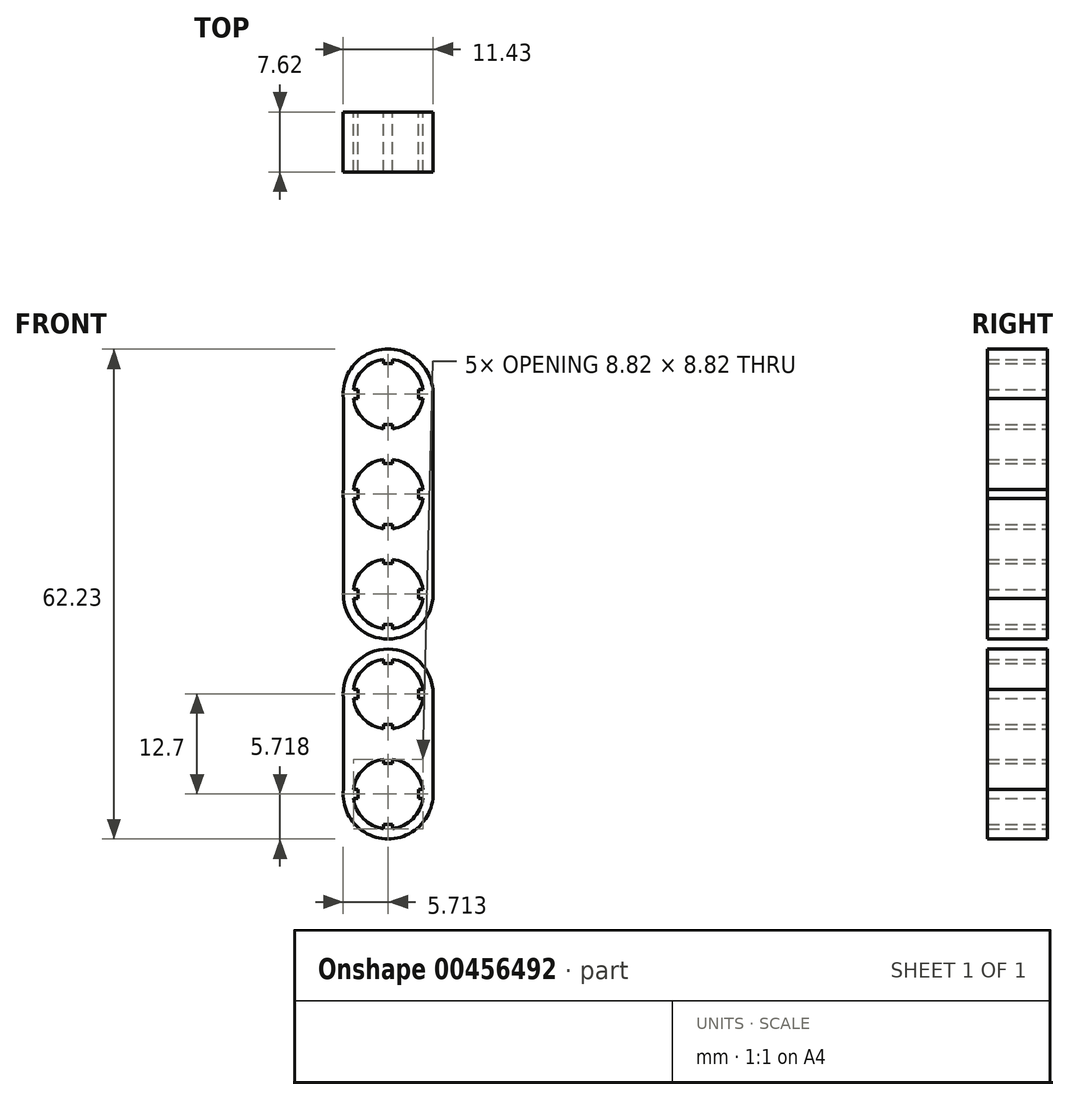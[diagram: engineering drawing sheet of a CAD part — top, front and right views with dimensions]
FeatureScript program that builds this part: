
annotation { "Feature Type Name" : "Feature", "Feature Type Description" : "" }
export const myFeature = defineFeature(function(context is Context, id is Id, definition is map)
    precondition{}
    {
        {
            var Q0;
            Q0=qCreatedBy(makeId("Front.planeOp"),FACE);
            var sketch = newSketch(context, id + "F0", { "sketchPlane" : qUnion([Q0])});
            skCircle(sketch, "E0", {"center": v(-13.53, 8.26) * mm, "radius": 4.45 * mm});
            skCircle(sketch, "E1", {"center": v(-13.53, -4.44) * mm, "radius": 4.45 * mm});
            skCircle(sketch, "E2", {"center": v(-13.53, -17.14) * mm, "radius": 4.45 * mm});
            skCircle(sketch, "E3", {"center": v(-13.53, -29.84) * mm, "radius": 4.45 * mm});
            skCircle(sketch, "E4", {"center": v(-13.53, -42.54) * mm, "radius": 4.45 * mm});
            skCircle(sketch, "E5", {"center": v(-13.53, 8.26) * mm, "radius": 5.72 * mm});
            skCircle(sketch, "E6", {"center": v(-13.53, -4.44) * mm, "radius": 5.72 * mm});
            skCircle(sketch, "E7", {"center": v(-13.53, -17.14) * mm, "radius": 5.72 * mm});
            skCircle(sketch, "E8", {"center": v(-13.53, -29.84) * mm, "radius": 5.72 * mm});
            skCircle(sketch, "E9", {"center": v(-13.53, -42.54) * mm, "radius": 5.72 * mm});
            skLineSegment(sketch, "E10", {"start": v(-18.03, 8.83) * mm, "end": v(-17.38, 8.83) * mm});
            skLineSegment(sketch, "E11", {"start": v(-17.38, 8.83) * mm, "end": v(-17.38, 7.69) * mm});
            skLineSegment(sketch, "E12", {"start": v(-17.38, 7.69) * mm, "end": v(-17.94, 7.69) * mm});
            skLineSegment(sketch, "E13", {"start": v(-9.12, -41.97) * mm, "end": v(-9.68, -41.97) * mm});
            skLineSegment(sketch, "E14", {"start": v(-9.68, -41.97) * mm, "end": v(-9.68, -43.11) * mm});
            skLineSegment(sketch, "E15", {"start": v(-9.68, -43.11) * mm, "end": v(-9.12, -43.11) * mm});
            skLineSegment(sketch, "E16", {"start": v(-9.12, 8.83) * mm, "end": v(-9.68, 8.83) * mm});
            skLineSegment(sketch, "E17", {"start": v(-9.68, 8.83) * mm, "end": v(-9.68, 7.69) * mm});
            skLineSegment(sketch, "E18", {"start": v(-9.68, 7.69) * mm, "end": v(-9.12, 7.69) * mm});
            skLineSegment(sketch, "E19", {"start": v(-14.1, 12.67) * mm, "end": v(-14.1, 12.1) * mm});
            skLineSegment(sketch, "E20", {"start": v(-14.1, 12.1) * mm, "end": v(-12.96, 12.1) * mm});
            skLineSegment(sketch, "E21", {"start": v(-12.96, 12.1) * mm, "end": v(-12.96, 12.67) * mm});
            skLineSegment(sketch, "E22", {"start": v(-14.1, 3.85) * mm, "end": v(-14.1, 4.4) * mm});
            skLineSegment(sketch, "E23", {"start": v(-14.1, 4.4) * mm, "end": v(-12.96, 4.4) * mm});
            skLineSegment(sketch, "E24", {"start": v(-12.96, 4.4) * mm, "end": v(-12.96, 3.85) * mm});
            skLineSegment(sketch, "E25", {"start": v(-14.1, -0.03) * mm, "end": v(-14.1, -0.6) * mm});
            skLineSegment(sketch, "E26", {"start": v(-14.1, -0.6) * mm, "end": v(-12.96, -0.6) * mm});
            skLineSegment(sketch, "E27", {"start": v(-12.96, -0.6) * mm, "end": v(-12.96, -0.03) * mm});
            skLineSegment(sketch, "E28", {"start": v(-14.1, -8.85) * mm, "end": v(-14.1, -8.3) * mm});
            skLineSegment(sketch, "E29", {"start": v(-14.1, -8.3) * mm, "end": v(-12.96, -8.3) * mm});
            skLineSegment(sketch, "E30", {"start": v(-12.96, -8.3) * mm, "end": v(-12.96, -8.85) * mm});
            skLineSegment(sketch, "E31", {"start": v(-17.94, -3.87) * mm, "end": v(-17.38, -3.87) * mm});
            skLineSegment(sketch, "E32", {"start": v(-17.38, -3.87) * mm, "end": v(-17.38, -5.01) * mm});
            skLineSegment(sketch, "E33", {"start": v(-17.38, -5.01) * mm, "end": v(-17.94, -5.01) * mm});
            skLineSegment(sketch, "E34", {"start": v(-9.12, -3.87) * mm, "end": v(-9.68, -3.87) * mm});
            skLineSegment(sketch, "E35", {"start": v(-9.68, -3.87) * mm, "end": v(-9.68, -5.01) * mm});
            skLineSegment(sketch, "E36", {"start": v(-9.68, -5.01) * mm, "end": v(-9.12, -5.01) * mm});
            skLineSegment(sketch, "E37", {"start": v(-14.1, -12.73) * mm, "end": v(-14.1, -13.3) * mm});
            skLineSegment(sketch, "E38", {"start": v(-14.1, -13.3) * mm, "end": v(-12.96, -13.3) * mm});
            skLineSegment(sketch, "E39", {"start": v(-12.96, -13.3) * mm, "end": v(-12.96, -12.73) * mm});
            skLineSegment(sketch, "E40", {"start": v(-14.1, -21.55) * mm, "end": v(-14.1, -21) * mm});
            skLineSegment(sketch, "E41", {"start": v(-14.1, -21) * mm, "end": v(-12.96, -21) * mm});
            skLineSegment(sketch, "E42", {"start": v(-12.96, -21) * mm, "end": v(-12.96, -21.55) * mm});
            skLineSegment(sketch, "E43", {"start": v(-17.94, -16.57) * mm, "end": v(-17.38, -16.57) * mm});
            skLineSegment(sketch, "E44", {"start": v(-17.38, -16.57) * mm, "end": v(-17.38, -17.71) * mm});
            skLineSegment(sketch, "E45", {"start": v(-17.38, -17.71) * mm, "end": v(-17.94, -17.71) * mm});
            skLineSegment(sketch, "E46", {"start": v(-9.12, -16.57) * mm, "end": v(-9.68, -16.57) * mm});
            skLineSegment(sketch, "E47", {"start": v(-9.68, -16.57) * mm, "end": v(-9.68, -17.71) * mm});
            skLineSegment(sketch, "E48", {"start": v(-9.68, -17.71) * mm, "end": v(-9.12, -17.71) * mm});
            skLineSegment(sketch, "E49", {"start": v(-14.1, -25.43) * mm, "end": v(-14.1, -26) * mm});
            skLineSegment(sketch, "E50", {"start": v(-14.1, -26) * mm, "end": v(-12.96, -26) * mm});
            skLineSegment(sketch, "E51", {"start": v(-12.96, -26) * mm, "end": v(-12.96, -25.43) * mm});
            skLineSegment(sketch, "E52", {"start": v(-14.1, -34.25) * mm, "end": v(-14.1, -33.7) * mm});
            skLineSegment(sketch, "E53", {"start": v(-14.1, -33.7) * mm, "end": v(-12.96, -33.7) * mm});
            skLineSegment(sketch, "E54", {"start": v(-12.96, -33.7) * mm, "end": v(-12.96, -34.25) * mm});
            skLineSegment(sketch, "E55", {"start": v(-17.94, -29.27) * mm, "end": v(-17.38, -29.27) * mm});
            skLineSegment(sketch, "E56", {"start": v(-17.38, -29.27) * mm, "end": v(-17.38, -30.41) * mm});
            skLineSegment(sketch, "E57", {"start": v(-17.38, -30.41) * mm, "end": v(-17.94, -30.41) * mm});
            skLineSegment(sketch, "E58", {"start": v(-9.12, -29.27) * mm, "end": v(-9.68, -29.27) * mm});
            skLineSegment(sketch, "E59", {"start": v(-9.68, -29.27) * mm, "end": v(-9.68, -30.41) * mm});
            skLineSegment(sketch, "E60", {"start": v(-9.68, -30.41) * mm, "end": v(-9.12, -30.41) * mm});
            skLineSegment(sketch, "E61", {"start": v(-17.94, -41.97) * mm, "end": v(-17.38, -41.97) * mm});
            skLineSegment(sketch, "E62", {"start": v(-17.38, -41.97) * mm, "end": v(-17.38, -43.11) * mm});
            skLineSegment(sketch, "E63", {"start": v(-17.38, -43.11) * mm, "end": v(-17.94, -43.11) * mm});
            skLineSegment(sketch, "E64", {"start": v(-14.1, -38.13) * mm, "end": v(-14.1, -38.7) * mm});
            skLineSegment(sketch, "E65", {"start": v(-14.1, -38.7) * mm, "end": v(-12.96, -38.7) * mm});
            skLineSegment(sketch, "E66", {"start": v(-12.96, -38.7) * mm, "end": v(-12.96, -38.13) * mm});
            skLineSegment(sketch, "E67", {"start": v(-14.1, -46.95) * mm, "end": v(-14.1, -46.4) * mm});
            skLineSegment(sketch, "E68", {"start": v(-14.1, -46.4) * mm, "end": v(-12.96, -46.4) * mm});
            skLineSegment(sketch, "E69", {"start": v(-12.96, -46.4) * mm, "end": v(-12.96, -46.95) * mm});
            skLineSegment(sketch, "E70", {"start": v(-19.21, 8.83) * mm, "end": v(-19.21, -42.54) * mm});
            skLineSegment(sketch, "E71", {"start": v(-19.21, -42.54) * mm, "end": v(-19.32, -43.49) * mm});
            skLineSegment(sketch, "E72", {"start": v(-7.84, 8.83) * mm, "end": v(-7.84, -43.11) * mm});
            skLineSegment(sketch, "E73", {"start": v(-7.84, -43.11) * mm, "end": v(-7.23, -42.43) * mm});
            skSolve(sketch);
        }
        {
            var Q0;
            {var subQ0=sQuery(id+"F0.wireOp",EDGE,"E70");var subQ1=sQuery(id+"F0.wireOp",EDGE,"E6");var subQ2=makeQuery(id+"F0.imprint","INTERSECT",VERTEX,{"disambiguationData":[OD(1.0)],"derivedFrom":[subQ1,subQ0]});Q0=makeQuery(id+"F0.imprint","IMPRINT",FACE,{"disambiguationData":[TD([[makeQuery(id+"F0.imprint","IMPRINT",EDGE,{"disambiguationData":[TD([[subQ2,-1.0]])],"derivedFrom":subQ1}),-1.0]])]});}
            var Q1;
            {var subQ0=sQuery(id+"F0.wireOp",EDGE,"E1");var subQ11=makeQuery(id+"F0.imprint","INTERSECT",VERTEX,{"derivedFrom":[subQ0,sQuery(id+"F0.wireOp",EDGE,"E27")]});Q1=makeQuery(id+"F0.imprint","IMPRINT",FACE,{"disambiguationData":[TD([[makeQuery(id+"F0.imprint","IMPRINT",EDGE,{"disambiguationData":[TD([[subQ11,1.0]])],"derivedFrom":subQ0}),-1.0]])]});}
            var Q2;
            {var subQ0=sQuery(id+"F0.wireOp",EDGE,"E70");var subQ1=sQuery(id+"F0.wireOp",EDGE,"E8");var subQ2=makeQuery(id+"F0.imprint","INTERSECT",VERTEX,{"disambiguationData":[OD(1.0)],"derivedFrom":[subQ1,subQ0]});Q2=makeQuery(id+"F0.imprint","IMPRINT",FACE,{"disambiguationData":[TD([[makeQuery(id+"F0.imprint","IMPRINT",EDGE,{"disambiguationData":[TD([[subQ2,-1.0]])],"derivedFrom":subQ1}),-1.0]])]});}
            var Q3;
            {var subQ5=sQuery(id+"F0.wireOp",EDGE,"E3");var subQ13=makeQuery(id+"F0.imprint","INTERSECT",VERTEX,{"derivedFrom":[subQ5,sQuery(id+"F0.wireOp",EDGE,"E51")]});Q3=makeQuery(id+"F0.imprint","IMPRINT",FACE,{"disambiguationData":[TD([[makeQuery(id+"F0.imprint","IMPRINT",EDGE,{"disambiguationData":[TD([[subQ13,1.0]])],"derivedFrom":subQ5}),-1.0]])]});}
            var Q4;
            {var subQ0=sQuery(id+"F0.wireOp",EDGE,"E70");var subQ1=sQuery(id+"F0.wireOp",EDGE,"E5");var subQ2=makeQuery(id+"F0.imprint","INTERSECT",VERTEX,{"disambiguationData":[OD(1.0)],"derivedFrom":[subQ1,subQ0]});Q4=makeQuery(id+"F0.imprint","IMPRINT",FACE,{"disambiguationData":[TD([[makeQuery(id+"F0.imprint","IMPRINT",EDGE,{"disambiguationData":[TD([[subQ2,-1.0]])],"derivedFrom":subQ1}),-1.0]])]});}
            var Q5;
            {var subQ0=sQuery(id+"F0.wireOp",EDGE,"E70");var subQ1=sQuery(id+"F0.wireOp",EDGE,"E7");var subQ2=makeQuery(id+"F0.imprint","INTERSECT",VERTEX,{"disambiguationData":[OD(1.0)],"derivedFrom":[subQ1,subQ0]});Q5=makeQuery(id+"F0.imprint","IMPRINT",FACE,{"disambiguationData":[TD([[makeQuery(id+"F0.imprint","IMPRINT",EDGE,{"disambiguationData":[TD([[subQ2,-1.0]])],"derivedFrom":subQ1}),-1.0]])]});}
            var Q6;
            {var subQ5=sQuery(id+"F0.wireOp",EDGE,"E2");var subQ11=makeQuery(id+"F0.imprint","INTERSECT",VERTEX,{"derivedFrom":[subQ5,sQuery(id+"F0.wireOp",EDGE,"E39")]});Q6=makeQuery(id+"F0.imprint","IMPRINT",FACE,{"disambiguationData":[TD([[makeQuery(id+"F0.imprint","IMPRINT",EDGE,{"disambiguationData":[TD([[subQ11,1.0]])],"derivedFrom":subQ5}),-1.0]])]});}
            var Q7;
            {var subQ7=sQuery(id+"F0.wireOp",EDGE,"E0");var subQ8=makeQuery(id+"F0.imprint","INTERSECT",VERTEX,{"derivedFrom":[subQ7,sQuery(id+"F0.wireOp",EDGE,"E16")]});Q7=makeQuery(id+"F0.imprint","IMPRINT",FACE,{"disambiguationData":[TD([[makeQuery(id+"F0.imprint","IMPRINT",EDGE,{"disambiguationData":[TD([[subQ8,-1.0]])],"derivedFrom":subQ7}),-1.0]])]});}
            var Q8;
            {var subQ0=sQuery(id+"F0.wireOp",EDGE,"E4");var subQ1=makeQuery(id+"F0.imprint","INTERSECT",VERTEX,{"derivedFrom":[subQ0,sQuery(id+"F0.wireOp",EDGE,"E13")]});Q8=makeQuery(id+"F0.imprint","IMPRINT",FACE,{"disambiguationData":[TD([[makeQuery(id+"F0.imprint","IMPRINT",EDGE,{"disambiguationData":[TD([[subQ1,-1.0]])],"derivedFrom":subQ0}),-1.0]])]});}
            var Q9;
            {var subQ0=sQuery(id+"F0.wireOp",EDGE,"E49");Q9=makeQuery(id+"F0.imprint","IMPRINT",FACE,{"disambiguationData":[TD([[makeQuery(id+"F0.imprint","IMPRINT",EDGE,{"derivedFrom":subQ0}),1.0]])]});}
            var Q10;
            {var subQ0=sQuery(id+"F0.wireOp",EDGE,"E70");var subQ1=sQuery(id+"F0.wireOp",EDGE,"E5");var subQ2=makeQuery(id+"F0.imprint","INTERSECT",VERTEX,{"disambiguationData":[OD(0.0)],"derivedFrom":[subQ1,subQ0]});Q10=makeQuery(id+"F0.imprint","IMPRINT",FACE,{"disambiguationData":[TD([[makeQuery(id+"F0.imprint","IMPRINT",EDGE,{"disambiguationData":[TD([[subQ2,-1.0]])],"derivedFrom":subQ1}),1.0]])]});}
            var Q11;
            {var subQ0=sQuery(id+"F0.wireOp",EDGE,"E72");var subQ1=sQuery(id+"F0.wireOp",EDGE,"E5");var subQ2=makeQuery(id+"F0.imprint","INTERSECT",VERTEX,{"disambiguationData":[OD(0.0)],"derivedFrom":[subQ1,subQ0]});Q11=makeQuery(id+"F0.imprint","IMPRINT",FACE,{"disambiguationData":[TD([[makeQuery(id+"F0.imprint","IMPRINT",EDGE,{"disambiguationData":[TD([[subQ2,1.0]])],"derivedFrom":subQ1}),1.0]])]});}
            var Q12;
            {var subQ0=sQuery(id+"F0.wireOp",EDGE,"E70");var subQ1=sQuery(id+"F0.wireOp",EDGE,"E6");var subQ2=makeQuery(id+"F0.imprint","INTERSECT",VERTEX,{"disambiguationData":[OD(0.0)],"derivedFrom":[subQ1,subQ0]});Q12=makeQuery(id+"F0.imprint","IMPRINT",FACE,{"disambiguationData":[TD([[makeQuery(id+"F0.imprint","IMPRINT",EDGE,{"disambiguationData":[TD([[subQ2,-1.0]])],"derivedFrom":subQ1}),1.0]])]});}
            var Q13;
            {var subQ0=sQuery(id+"F0.wireOp",EDGE,"E72");var subQ1=sQuery(id+"F0.wireOp",EDGE,"E7");var subQ2=makeQuery(id+"F0.imprint","INTERSECT",VERTEX,{"disambiguationData":[OD(0.0)],"derivedFrom":[subQ1,subQ0]});Q13=makeQuery(id+"F0.imprint","IMPRINT",FACE,{"disambiguationData":[TD([[makeQuery(id+"F0.imprint","IMPRINT",EDGE,{"disambiguationData":[TD([[subQ2,1.0]])],"derivedFrom":subQ1}),1.0]])]});}
            var Q14;
            {var subQ0=sQuery(id+"F0.wireOp",EDGE,"E72");var subQ1=sQuery(id+"F0.wireOp",EDGE,"E9");var subQ2=makeQuery(id+"F0.imprint","INTERSECT",VERTEX,{"disambiguationData":[OD(0.0)],"derivedFrom":[subQ1,subQ0]});Q14=makeQuery(id+"F0.imprint","IMPRINT",FACE,{"disambiguationData":[TD([[makeQuery(id+"F0.imprint","IMPRINT",EDGE,{"disambiguationData":[TD([[subQ2,-1.0]])],"derivedFrom":subQ1}),1.0]])]});}
            var Q15;
            {var subQ0=sQuery(id+"F0.wireOp",EDGE,"E37");Q15=makeQuery(id+"F0.imprint","IMPRINT",FACE,{"disambiguationData":[TD([[makeQuery(id+"F0.imprint","IMPRINT",EDGE,{"derivedFrom":subQ0}),1.0]])]});}
            var Q16;
            {var subQ0=sQuery(id+"F0.wireOp",EDGE,"E25");Q16=makeQuery(id+"F0.imprint","IMPRINT",FACE,{"disambiguationData":[TD([[makeQuery(id+"F0.imprint","IMPRINT",EDGE,{"derivedFrom":subQ0}),1.0]])]});}
            var Q17;
            {var subQ0=sQuery(id+"F0.wireOp",EDGE,"E64");Q17=makeQuery(id+"F0.imprint","IMPRINT",FACE,{"disambiguationData":[TD([[makeQuery(id+"F0.imprint","IMPRINT",EDGE,{"derivedFrom":subQ0}),1.0]])]});}
            var Q18;
            {var subQ0=sQuery(id+"F0.wireOp",EDGE,"E72");var subQ1=sQuery(id+"F0.wireOp",EDGE,"E6");var subQ2=makeQuery(id+"F0.imprint","INTERSECT",VERTEX,{"disambiguationData":[OD(0.0)],"derivedFrom":[subQ1,subQ0]});Q18=makeQuery(id+"F0.imprint","IMPRINT",FACE,{"disambiguationData":[TD([[makeQuery(id+"F0.imprint","IMPRINT",EDGE,{"disambiguationData":[TD([[subQ2,1.0]])],"derivedFrom":subQ1}),1.0]])]});}
            var Q19;
            {var subQ0=sQuery(id+"F0.wireOp",EDGE,"E70");var subQ1=sQuery(id+"F0.wireOp",EDGE,"E7");var subQ2=makeQuery(id+"F0.imprint","INTERSECT",VERTEX,{"disambiguationData":[OD(0.0)],"derivedFrom":[subQ1,subQ0]});Q19=makeQuery(id+"F0.imprint","IMPRINT",FACE,{"disambiguationData":[TD([[makeQuery(id+"F0.imprint","IMPRINT",EDGE,{"disambiguationData":[TD([[subQ2,-1.0]])],"derivedFrom":subQ1}),1.0]])]});}
            var Q20;
            {var subQ0=sQuery(id+"F0.wireOp",EDGE,"E70");var subQ1=sQuery(id+"F0.wireOp",EDGE,"E8");var subQ2=makeQuery(id+"F0.imprint","INTERSECT",VERTEX,{"disambiguationData":[OD(0.0)],"derivedFrom":[subQ1,subQ0]});Q20=makeQuery(id+"F0.imprint","IMPRINT",FACE,{"disambiguationData":[TD([[makeQuery(id+"F0.imprint","IMPRINT",EDGE,{"disambiguationData":[TD([[subQ2,-1.0]])],"derivedFrom":subQ1}),1.0]])]});}
            var Q21;
            {var subQ0=sQuery(id+"F0.wireOp",EDGE,"E72");var subQ1=sQuery(id+"F0.wireOp",EDGE,"E8");var subQ2=makeQuery(id+"F0.imprint","INTERSECT",VERTEX,{"disambiguationData":[OD(0.0)],"derivedFrom":[subQ1,subQ0]});Q21=makeQuery(id+"F0.imprint","IMPRINT",FACE,{"disambiguationData":[TD([[makeQuery(id+"F0.imprint","IMPRINT",EDGE,{"disambiguationData":[TD([[subQ2,1.0]])],"derivedFrom":subQ1}),1.0]])]});}
            var Q22;
            {var subQ0=sQuery(id+"F0.wireOp",EDGE,"E19");Q22=makeQuery(id+"F0.imprint","IMPRINT",FACE,{"disambiguationData":[TD([[makeQuery(id+"F0.imprint","IMPRINT",EDGE,{"derivedFrom":subQ0}),1.0]])]});}
            var Q23;
            {var subQ0=sQuery(id+"F0.wireOp",EDGE,"E71");var subQ1=sQuery(id+"F0.wireOp",EDGE,"E9");var subQ2=makeQuery(id+"F0.imprint","INTERSECT",VERTEX,{"derivedFrom":[subQ1,subQ0]});Q23=makeQuery(id+"F0.imprint","IMPRINT",FACE,{"disambiguationData":[TD([[makeQuery(id+"F0.imprint","IMPRINT",EDGE,{"disambiguationData":[TD([[subQ2,1.0]])],"derivedFrom":subQ1}),1.0]])]});}
            var Q24;
            {var subQ0=sQuery(id+"F0.wireOp",EDGE,"E58");Q24=makeQuery(id+"F0.imprint","IMPRINT",FACE,{"disambiguationData":[TD([[makeQuery(id+"F0.imprint","IMPRINT",EDGE,{"derivedFrom":subQ0}),1.0]])]});}
            var Q25;
            {var subQ0=sQuery(id+"F0.wireOp",EDGE,"E55");Q25=makeQuery(id+"F0.imprint","IMPRINT",FACE,{"disambiguationData":[TD([[makeQuery(id+"F0.imprint","IMPRINT",EDGE,{"derivedFrom":subQ0}),-1.0]])]});}
            var Q26;
            {var subQ0=sQuery(id+"F0.wireOp",EDGE,"E34");Q26=makeQuery(id+"F0.imprint","IMPRINT",FACE,{"disambiguationData":[TD([[makeQuery(id+"F0.imprint","IMPRINT",EDGE,{"derivedFrom":subQ0}),1.0]])]});}
            var Q27;
            {var subQ0=sQuery(id+"F0.wireOp",EDGE,"E40");Q27=makeQuery(id+"F0.imprint","IMPRINT",FACE,{"disambiguationData":[TD([[makeQuery(id+"F0.imprint","IMPRINT",EDGE,{"derivedFrom":subQ0}),-1.0]])]});}
            var Q28;
            {var subQ0=sQuery(id+"F0.wireOp",EDGE,"E61");Q28=makeQuery(id+"F0.imprint","IMPRINT",FACE,{"disambiguationData":[TD([[makeQuery(id+"F0.imprint","IMPRINT",EDGE,{"derivedFrom":subQ0}),-1.0]])]});}
            var Q29;
            {var subQ0=sQuery(id+"F0.wireOp",EDGE,"E46");Q29=makeQuery(id+"F0.imprint","IMPRINT",FACE,{"disambiguationData":[TD([[makeQuery(id+"F0.imprint","IMPRINT",EDGE,{"derivedFrom":subQ0}),1.0]])]});}
            var Q30;
            {var subQ0=sQuery(id+"F0.wireOp",EDGE,"E67");Q30=makeQuery(id+"F0.imprint","IMPRINT",FACE,{"disambiguationData":[TD([[makeQuery(id+"F0.imprint","IMPRINT",EDGE,{"derivedFrom":subQ0}),-1.0]])]});}
            var Q31;
            {var subQ0=sQuery(id+"F0.wireOp",EDGE,"E31");Q31=makeQuery(id+"F0.imprint","IMPRINT",FACE,{"disambiguationData":[TD([[makeQuery(id+"F0.imprint","IMPRINT",EDGE,{"derivedFrom":subQ0}),-1.0]])]});}
            var Q32;
            {var subQ0=sQuery(id+"F0.wireOp",EDGE,"E16");Q32=makeQuery(id+"F0.imprint","IMPRINT",FACE,{"disambiguationData":[TD([[makeQuery(id+"F0.imprint","IMPRINT",EDGE,{"derivedFrom":subQ0}),1.0]])]});}
            var Q33;
            {var subQ0=sQuery(id+"F0.wireOp",EDGE,"E28");Q33=makeQuery(id+"F0.imprint","IMPRINT",FACE,{"disambiguationData":[TD([[makeQuery(id+"F0.imprint","IMPRINT",EDGE,{"derivedFrom":subQ0}),-1.0]])]});}
            var Q34;
            {var subQ0=sQuery(id+"F0.wireOp",EDGE,"E43");Q34=makeQuery(id+"F0.imprint","IMPRINT",FACE,{"disambiguationData":[TD([[makeQuery(id+"F0.imprint","IMPRINT",EDGE,{"derivedFrom":subQ0}),-1.0]])]});}
            var Q35;
            {var subQ4=sQuery(id+"F0.wireOp",EDGE,"E11");Q35=makeQuery(id+"F0.imprint","IMPRINT",FACE,{"disambiguationData":[TD([[makeQuery(id+"F0.imprint","IMPRINT",EDGE,{"derivedFrom":subQ4}),-1.0]])]});}
            var Q36;
            {var subQ0=sQuery(id+"F0.wireOp",EDGE,"E22");Q36=makeQuery(id+"F0.imprint","IMPRINT",FACE,{"disambiguationData":[TD([[makeQuery(id+"F0.imprint","IMPRINT",EDGE,{"derivedFrom":subQ0}),-1.0]])]});}
            var Q37;
            {var subQ0=sQuery(id+"F0.wireOp",EDGE,"E13");Q37=makeQuery(id+"F0.imprint","IMPRINT",FACE,{"disambiguationData":[TD([[makeQuery(id+"F0.imprint","IMPRINT",EDGE,{"derivedFrom":subQ0}),1.0]])]});}
            var Q38;
            {var subQ0=sQuery(id+"F0.wireOp",EDGE,"E52");Q38=makeQuery(id+"F0.imprint","IMPRINT",FACE,{"disambiguationData":[TD([[makeQuery(id+"F0.imprint","IMPRINT",EDGE,{"derivedFrom":subQ0}),-1.0]])]});}
            extrude(context, id + "F1", {"entities" : qUnion([Q0, Q1, Q2, Q3, Q4, Q5, Q6, Q7, Q8, Q9, Q10, Q11, Q12, Q13, Q14, Q15, Q16, Q17, Q18, Q19, Q20, Q21, Q22, Q23, Q24, Q25, Q26, Q27, Q28, Q29, Q30, Q31, Q32, Q33, Q34, Q35, Q36, Q37, Q38]), "depth" : 7.62 * mm, "offsetDistance" : 25.4 * mm});
        }
    });
